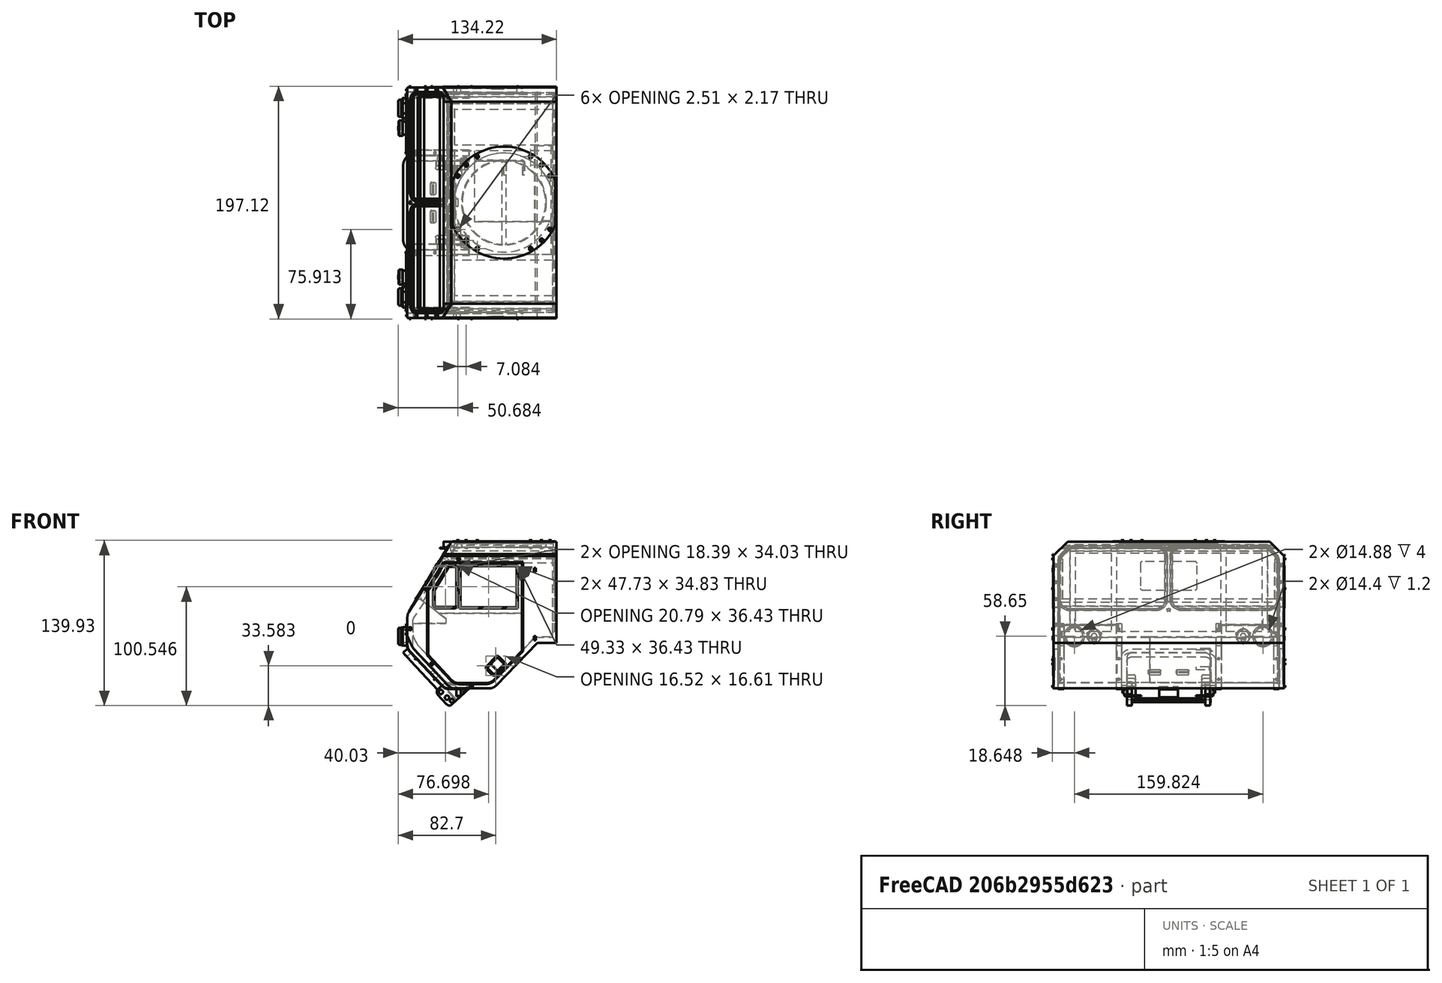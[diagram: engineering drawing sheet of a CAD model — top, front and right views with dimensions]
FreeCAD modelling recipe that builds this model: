
FCSTD DOCUMENT  (FreeCAD 0.16R6188 (Git))
Label: hemtt
License: All rights reserved
LicenseURL: http://en.wikipedia.org/wiki/All_rights_reserved
objects: Sketcher::SketchObject×10, Part::Feature×7, PartDesign::Pad×7, Part::MultiFuse×7, Part::Cut×5, Part::Box×2, Part::FeaturePython×1, Part::Mirroring×1, Part::MultiCommon×1
note: 48 computed .brp shape members not serialized (recipe doc carries the construction recipe); baked Part::Feature solids carry a one-line shape summary decoded from their .brp

FEATURE [Part::Feature] Part__Feature025  label="TELAIO HMTT025"
  shape: bbox 10530 x 1984 x 2594 mm, 1907 faces (baked)
FEATURE [Part::Feature] Part__Feature054  label="FARO CON CARTER002"
  Placement = pos=(-2615,1569,-998.9) rot=(0.707107,0,-0.707107;3.14159rad)
  shape: bbox 45 x 194.8 x 194.8 mm, 8 faces (baked)
FEATURE [Part::Feature] Part__Feature052  label="FARO CON CARTER"
  Placement = pos=(-2615,1569,998.9) rot=(-0.57735,0.57735,0.57735;4.18879rad)
  shape: bbox 45 x 194.8 x 194.8 mm, 8 faces (baked)
FEATURE [Part::Feature] Part__Feature057  label="LUCE NOTTURNA001"
  Placement = pos=(-2610,1569,-788.9) rot=(0,-1,0;1.5708rad)
  shape: bbox 99 x 164.8 x 161.2 mm, 70 faces (baked)
FEATURE [Part::Feature] Part__Feature059  label="LUCE NOTTURNA003"
  Placement = pos=(-2610,1569,788.9) rot=(0,-1,0;1.5708rad)
  shape: bbox 99 x 164.8 x 161.2 mm, 70 faces (baked)
FEATURE [Sketcher::SketchObject] Sketch
  Placement = pos=(0,-100,0) rot=(-1,0,0;4.71239rad)
  sketch-geometry (9):
    g0: LineSegment StartX=-82.586 StartY=78.6056 StartZ=0 EndX=-89.3602 EndY=104.808 EndZ=0
    g1: LineSegment StartX=-89.3602 StartY=104.808 StartZ=0 EndX=-99.131 EndY=104.808 EndZ=0
    g2: LineSegment StartX=-99.131 StartY=104.808 StartZ=0 EndX=-99.131 EndY=54.1502 EndZ=0
    g3: LineSegment StartX=-99.131 StartY=54.1502 StartZ=0 EndX=-82.0275 EndY=58.4399 EndZ=0
    g4: LineSegment StartX=-82.0275 StartY=58.4399 StartZ=0 EndX=-82.0275 EndY=60.6882 EndZ=0
    g5: LineSegment StartX=-82.0275 StartY=60.6882 StartZ=0 EndX=-90.9811 EndY=60.6882 EndZ=0
    g6: LineSegment StartX=-90.9811 StartY=60.6882 StartZ=0 EndX=-90.9811 EndY=76.174 EndZ=0
    g7: LineSegment StartX=-90.9811 StartY=76.174 StartZ=0 EndX=-82.586 EndY=76.174 EndZ=0
    g8: LineSegment StartX=-82.586 StartY=76.174 StartZ=0 EndX=-82.586 EndY=78.6056 EndZ=0
  constraints (16):
    c: Coincident(g0,g1)
    c: Horizontal(g1)
    c: Coincident(g1,g2)
    c: Vertical(g2)
    c: Coincident(g2,g3)
    c: Coincident(g3,g4)
    c: Vertical(g4)
    c: Coincident(g5,g4)
    c: Horizontal(g5)
    c: Coincident(g5,g6)
    c: Vertical(g6)
    c: Coincident(g6,g7)
    c: Horizontal(g7)
    c: Coincident(g7,g8)
    c: Coincident(g8,g0)
    c: Vertical(g8)
FEATURE [PartDesign::Pad] Pad
  Length = 210
  Length2 = 100
  Placement = pos=(0,-100,0) rot=(-1,0,0;4.71239rad)
  Reversed = true
  Sketch = -> Sketch
  Type = 0
FEATURE [Part::Feature] Part__Feature053  label="FARO CON CARTER001"
  Placement = pos=(-2615,1569,998.9) rot=(-0.57735,0.57735,0.57735;4.18879rad)
  shape: bbox 56 x 238.1 x 238.1 mm, 11 faces (baked)
FEATURE [Part::Feature] Part__Feature055  label="FARO CON CARTER003"
  Placement = pos=(-2615,1569,-998.9) rot=(0.707107,0,-0.707107;3.14159rad)
  shape: bbox 56 x 238.1 x 238.1 mm, 11 faces (baked)
FEATURE [Part::MultiFuse] Fusion
  Placement = pos=(0,0,0) rot=(1,0,0;1.5708rad)
  Shapes = -> [Part__Feature025,Part__Feature054,Part__Feature052,Part__Feature057,Part__Feature059,Part__Feature053,Part__Feature055]
FEATURE [Part::FeaturePython] Clone  label="Clone of Fusion"  # Draft clone (typed FeaturePython)
  Objects = -> [Fusion]
  Placement = pos=(120,0,-57) rot=(1,0,0;1.5708rad)
  Scale = (0.08,0.08,0.08)
FEATURE [Part::Cut] Cut
  Base = -> Clone
  Tool = -> Pad
FEATURE [Sketcher::SketchObject] Sketch001
  ExternalGeometry = -> [Cut]
  Placement = pos=(0,-97.6,0) rot=(1,0,0;1.5708rad)
  Support = -> Cut [Face30]
  sketch-geometry (11):
    g0: LineSegment StartX=-6.58206 StartY=26.7619 StartZ=0 EndX=28.4927 EndY=62.9077 EndZ=0
    g1: LineSegment StartX=28.4927 StartY=62.9077 StartZ=0 EndX=48.7262 EndY=62.9077 EndZ=0
    g2: LineSegment StartX=48.7262 StartY=62.9077 StartZ=0 EndX=48.7262 EndY=84.8524 EndZ=0
    g3: LineSegment StartX=48.7262 StartY=84.8524 StartZ=0 EndX=927.788 EndY=84.8524 EndZ=0
    g4: LineSegment StartX=927.788 StartY=84.8524 StartZ=0 EndX=927.788 EndY=-26.8754 EndZ=0
    g5: LineSegment StartX=927.788 StartY=-26.8754 StartZ=0 EndX=-68.5109 EndY=-26.8754 EndZ=0
    g6: LineSegment StartX=-68.5109 StartY=-26.8754 StartZ=0 EndX=-68.5109 EndY=-12.2515 EndZ=0
    g7: LineSegment StartX=-43.7868 StartY=10.7317 StartZ=0 EndX=-29.1551 EndY=24.3331 EndZ=0
    g8: LineSegment StartX=-29.1551 StartY=24.3331 StartZ=0 EndX=-12.3233 EndY=24.3331 EndZ=0
    g9: LineSegment StartX=-43.7868 StartY=10.7317 StartZ=0 EndX=-68.5109 EndY=-12.2515 EndZ=0
    g10: ArcOfCircle CenterX=-12.3233 CenterY=32.3331 CenterZ=0 NormalX=0 NormalY=0 NormalZ=1 Radius=8 StartAngle=4.71239 EndAngle=5.51282
  constraints (20):
    c: Coincident(g0,g1)
    c: Horizontal(g1)
    c: Coincident(g1,g2)
    c: Vertical(g2)
    c: Coincident(g2,g3)
    c: Horizontal(g3)
    c: Coincident(g3,g4)
    c: Vertical(g4)
    c: Coincident(g4,g5)
    c: Horizontal(g5)
    c: Coincident(g5,g6)
    c: Coincident(g7,g8)
    c: Horizontal(g8)
    c: Coincident(g7,g-4)
    c: Coincident(g9,g7)
    c: Coincident(g9,g6)
    c: Parallel(g9,g7)
    c: Vertical(g6)
    c: Coincident(g10,g0)
    c: Coincident(g10,g8)
FEATURE [Sketcher::SketchObject] Sketch003
  Placement = pos=(0,-101.6,0) rot=(1,0,0;1.5708rad)
  sketch-geometry (11):
    g0: LineSegment StartX=-6.58206 StartY=26.7619 StartZ=0 EndX=28.4927 EndY=62.9077 EndZ=0
    g1: LineSegment StartX=28.4927 StartY=62.9077 StartZ=0 EndX=48.7262 EndY=62.9077 EndZ=0
    g2: LineSegment StartX=48.7262 StartY=62.9077 StartZ=0 EndX=48.7262 EndY=84.8524 EndZ=0
    g3: LineSegment StartX=48.7262 StartY=84.8524 StartZ=0 EndX=927.788 EndY=84.8524 EndZ=0
    g4: LineSegment StartX=927.788 StartY=84.8524 StartZ=0 EndX=927.788 EndY=-26.8754 EndZ=0
    g5: LineSegment StartX=927.788 StartY=-26.8754 StartZ=0 EndX=-68.5109 EndY=-26.8754 EndZ=0
    g6: LineSegment StartX=-68.5109 StartY=-26.8754 StartZ=0 EndX=-68.5109 EndY=-12.2515 EndZ=0
    g7: LineSegment StartX=-43.7868 StartY=10.7317 StartZ=0 EndX=-29.1551 EndY=24.3331 EndZ=0
    g8: LineSegment StartX=-29.1551 StartY=24.3331 StartZ=0 EndX=-12.3233 EndY=24.3331 EndZ=0
    g9: LineSegment StartX=-43.7868 StartY=10.7317 StartZ=0 EndX=-68.5109 EndY=-12.2515 EndZ=0
    g10: ArcOfCircle CenterX=-12.3233 CenterY=32.3331 CenterZ=0 NormalX=0 NormalY=0 NormalZ=1 Radius=8 StartAngle=4.71239 EndAngle=5.51282
  constraints (19):
    c: Coincident(g0,g1)
    c: Horizontal(g1)
    c: Coincident(g1,g2)
    c: Vertical(g2)
    c: Coincident(g2,g3)
    c: Horizontal(g3)
    c: Coincident(g3,g4)
    c: Vertical(g4)
    c: Coincident(g4,g5)
    c: Horizontal(g5)
    c: Coincident(g5,g6)
    c: Coincident(g7,g8)
    c: Horizontal(g8)
    c: Coincident(g9,g7)
    c: Coincident(g9,g6)
    c: Parallel(g9,g7)
    c: Vertical(g6)
    c: Coincident(g10,g0)
    c: Coincident(g10,g8)
FEATURE [PartDesign::Pad] Pad001
  Length = 210
  Length2 = 100
  Placement = pos=(0,-101.6,0) rot=(1,0,0;1.5708rad)
  Reversed = true
  Sketch = -> Sketch003
  Type = 0
FEATURE [Part::Cut] Cut001
  Base = -> Cut
  Tool = -> Pad001
FEATURE [Sketcher::SketchObject] Sketch004
  ExternalGeometry = -> [Cut001]
  Placement = pos=(0,-97.6,0) rot=(1,0,0;1.5708rad)
  Support = -> Cut001 [Face749]
  sketch-geometry (24):
    g0: LineSegment StartX=11.0422 StartY=127.83 StartZ=0 EndX=-36.6868 EndY=127.83 EndZ=0
    g1: LineSegment StartX=-36.6868 StartY=127.83 StartZ=0 EndX=-36.6868 EndY=93.0022 EndZ=0
    g2: LineSegment StartX=-36.6868 StartY=93.0022 StartZ=0 EndX=11.0422 EndY=93.0022 EndZ=0
    g3: LineSegment StartX=11.0422 StartY=93.0022 StartZ=0 EndX=11.0422 EndY=127.83 EndZ=0
    g4: LineSegment StartX=-45.8126 StartY=127.43 StartZ=0 EndX=-41.4972 EndY=127.43 EndZ=0
    g5: ArcOfCircle CenterX=-45.8126 CenterY=126.23 CenterZ=0 NormalX=0 NormalY=0 NormalZ=1 Radius=1.2 StartAngle=1.5708 EndAngle=2.59824
    g6: ArcOfCircle CenterX=-41.4972 CenterY=126.23 CenterZ=0 NormalX=0 NormalY=0 NormalZ=1 Radius=1.2 StartAngle=0 EndAngle=1.5708
    g7: LineSegment StartX=-46.8398 StartY=126.851 StartZ=0 EndX=-58.5097 EndY=107.529 EndZ=0
    g8: LineSegment StartX=-40.2972 StartY=126.23 StartZ=0 EndX=-40.2972 EndY=94.6022 EndZ=0
    g9: LineSegment StartX=-58.6825 StartY=106.909 StartZ=0 EndX=-58.6825 EndY=94.6022 EndZ=0
    g10: LineSegment StartX=-57.4825 StartY=93.4022 StartZ=0 EndX=-41.4972 EndY=93.4022 EndZ=0
    g11: ArcOfCircle CenterX=-57.4825 CenterY=106.909 CenterZ=0 NormalX=0 NormalY=0 NormalZ=1 Radius=1.2 StartAngle=2.59824 EndAngle=3.14159
    g12: ArcOfCircle CenterX=-41.4972 CenterY=94.6022 CenterZ=0 NormalX=0 NormalY=0 NormalZ=1 Radius=1.2 StartAngle=4.71239 EndAngle=6.28319
    g13: ArcOfCircle CenterX=-57.4825 CenterY=94.6022 CenterZ=0 NormalX=0 NormalY=0 NormalZ=1 Radius=1.2 StartAngle=3.14159 EndAngle=4.71239
    g14: LineSegment StartX=-63.6825 StartY=88.0022 StartZ=0 EndX=-63.6825 EndY=108.636 EndZ=0
    g15: LineSegment StartX=-63.6825 StartY=108.636 StartZ=0 EndX=-49.0694 EndY=132.83 EndZ=0
    g16: LineSegment StartX=-49.0694 StartY=132.83 StartZ=0 EndX=16.0422 EndY=132.83 EndZ=0
    g17: LineSegment StartX=16.0422 StartY=132.83 StartZ=0 EndX=16.0422 EndY=88.0022 EndZ=0
    g18: LineSegment StartX=16.0422 StartY=88.0022 StartZ=0 EndX=-63.6825 EndY=88.0022 EndZ=0
    g19: LineSegment [constr] StartX=-36.6868 StartY=93.0022 StartZ=0 EndX=-36.6868 EndY=88.0022 EndZ=0
    g20: LineSegment [constr] StartX=-36.6868 StartY=127.83 StartZ=0 EndX=-36.6868 EndY=132.83 EndZ=0
    g21: LineSegment [constr] StartX=-46.8398 StartY=126.851 StartZ=0 EndX=-51.1197 EndY=129.436 EndZ=0
    g22: LineSegment [constr] StartX=11.0422 StartY=127.83 StartZ=0 EndX=16.0422 EndY=127.83 EndZ=0
    g23: LineSegment [constr] StartX=-58.6825 StartY=106.909 StartZ=0 EndX=-63.6825 EndY=106.909 EndZ=0
  constraints (65):
    c: Coincident(g0,g1)
    c: Coincident(g1,g2)
    c: Coincident(g2,g3)
    c: Coincident(g3,g0)
    c: Horizontal(g0)
    c: Horizontal(g2)
    c: Vertical(g1)
    c: Vertical(g3)
    c: Coincident(g0,g-9)
    c: Coincident(g1,g-8)
    c: Coincident(g-4,g4)
    c: Coincident(g-3,g4)
    c: Coincident(g5,g-3)
    c: Coincident(g5,g4)
    c: Coincident(g5,g-3)
    c: Coincident(g6,g-4)
    c: Coincident(g6,g4)
    c: Coincident(g6,g-4)
    c: Coincident(g7,g-6)
    c: Coincident(g5,g7)
    c: Coincident(g8,g6)
    c: Coincident(g8,g-7)
    c: Coincident(g9,g-6)
    c: Coincident(g9,g-5)
    c: Coincident(g10,g-5)
    c: Coincident(g10,g-7)
    c: Coincident(g11,g-6)
    c: Coincident(g11,g7)
    c: Coincident(g11,g9)
    c: Coincident(g12,g-7)
    c: Coincident(g12,g8)
    c: Coincident(g12,g10)
    c: Coincident(g13,g-5)
    c: Coincident(g13,g9)
    c: Coincident(g13,g10)
    c: Vertical(g14)
    c: Coincident(g14,g15)
    c: Coincident(g15,g16)
    c: Horizontal(g16)
    c: Coincident(g16,g17)
    c: Vertical(g17)
    c: Coincident(g17,g18)
    c: Coincident(g18,g14)
    c: Horizontal(g18)
    c: Coincident(g19,g1)
    c: PointOnObject(g19,g18)
    c: Vertical(g19)
    c: Coincident(g20,g0)
    c: PointOnObject(g20,g16)
    c: Vertical(g20)
    c: Coincident(g21,g5)
    c: PointOnObject(g21,g15)
    c: Coincident(g22,g0)
    c: PointOnObject(g22,g17)
    c: Horizontal(g22)
    c: Coincident(g23,g9)
    c: PointOnObject(g23,g14)
    c: Horizontal(g23)
    c: Perpendicular(g21,g15)
    c: Equal(g23,g21)
    c: Equal(g21,g20)
    c: Equal(g20,g22)
    c: Equal(g22,g19)
    c: Parallel(g15,g7)
    c: Distance(g20) = 5
FEATURE [Sketcher::SketchObject] Sketch007
  Placement = pos=(0,-97.5,0) rot=(1,0,0;1.5708rad)
  sketch-geometry (24):
    g0: LineSegment StartX=11.0422 StartY=127.83 StartZ=0 EndX=-36.6868 EndY=127.83 EndZ=0
    g1: LineSegment StartX=-36.6868 StartY=127.83 StartZ=0 EndX=-36.6868 EndY=93.0022 EndZ=0
    g2: LineSegment StartX=-36.6868 StartY=93.0022 StartZ=0 EndX=11.0422 EndY=93.0022 EndZ=0
    g3: LineSegment StartX=11.0422 StartY=93.0022 StartZ=0 EndX=11.0422 EndY=127.83 EndZ=0
    g4: LineSegment StartX=-45.8126 StartY=127.43 StartZ=0 EndX=-41.4972 EndY=127.43 EndZ=0
    g5: ArcOfCircle CenterX=-45.8126 CenterY=126.23 CenterZ=0 NormalX=0 NormalY=0 NormalZ=1 Radius=1.2 StartAngle=1.5708 EndAngle=2.59824
    g6: ArcOfCircle CenterX=-41.4972 CenterY=126.23 CenterZ=0 NormalX=0 NormalY=0 NormalZ=1 Radius=1.2 StartAngle=0 EndAngle=1.5708
    g7: LineSegment StartX=-46.8398 StartY=126.851 StartZ=0 EndX=-58.5097 EndY=107.529 EndZ=0
    g8: LineSegment StartX=-40.2972 StartY=126.23 StartZ=0 EndX=-40.2972 EndY=94.6022 EndZ=0
    g9: LineSegment StartX=-58.6825 StartY=106.909 StartZ=0 EndX=-58.6825 EndY=94.6022 EndZ=0
    g10: LineSegment StartX=-57.4825 StartY=93.4022 StartZ=0 EndX=-41.4972 EndY=93.4022 EndZ=0
    g11: ArcOfCircle CenterX=-57.4825 CenterY=106.909 CenterZ=0 NormalX=0 NormalY=0 NormalZ=1 Radius=1.2 StartAngle=2.59824 EndAngle=3.14159
    g12: ArcOfCircle CenterX=-41.4972 CenterY=94.6022 CenterZ=0 NormalX=0 NormalY=0 NormalZ=1 Radius=1.2 StartAngle=4.71239 EndAngle=6.28319
    g13: ArcOfCircle CenterX=-57.4825 CenterY=94.6022 CenterZ=0 NormalX=0 NormalY=0 NormalZ=1 Radius=1.2 StartAngle=3.14159 EndAngle=4.71239
    g14: LineSegment StartX=-63.6825 StartY=88.0022 StartZ=0 EndX=-63.6825 EndY=108.636 EndZ=0
    g15: LineSegment StartX=-63.6825 StartY=108.636 StartZ=0 EndX=-49.0694 EndY=132.83 EndZ=0
    g16: LineSegment StartX=-49.0694 StartY=132.83 StartZ=0 EndX=16.0422 EndY=132.83 EndZ=0
    g17: LineSegment StartX=16.0422 StartY=132.83 StartZ=0 EndX=16.0422 EndY=88.0022 EndZ=0
    g18: LineSegment StartX=16.0422 StartY=88.0022 StartZ=0 EndX=-63.6825 EndY=88.0022 EndZ=0
    g19: LineSegment [constr] StartX=-36.6868 StartY=93.0022 StartZ=0 EndX=-36.6868 EndY=88.0022 EndZ=0
    g20: LineSegment [constr] StartX=-36.6868 StartY=127.83 StartZ=0 EndX=-36.6868 EndY=132.83 EndZ=0
    g21: LineSegment [constr] StartX=-46.8398 StartY=126.851 StartZ=0 EndX=-51.1197 EndY=129.436 EndZ=0
    g22: LineSegment [constr] StartX=11.0422 StartY=127.83 StartZ=0 EndX=16.0422 EndY=127.83 EndZ=0
    g23: LineSegment [constr] StartX=-58.6825 StartY=106.909 StartZ=0 EndX=-63.6825 EndY=106.909 EndZ=0
  constraints (48):
    c: Coincident(g0,g1)
    c: Coincident(g1,g2)
    c: Coincident(g2,g3)
    c: Coincident(g3,g0)
    c: Horizontal(g0)
    c: Horizontal(g2)
    c: Vertical(g1)
    c: Vertical(g3)
    c: Coincident(g5,g4)
    c: Coincident(g6,g4)
    c: Coincident(g5,g7)
    c: Coincident(g8,g6)
    c: Coincident(g11,g7)
    c: Coincident(g11,g9)
    c: Coincident(g12,g8)
    c: Coincident(g12,g10)
    c: Coincident(g13,g9)
    c: Coincident(g13,g10)
    c: Vertical(g14)
    c: Coincident(g14,g15)
    c: Coincident(g15,g16)
    c: Horizontal(g16)
    c: Coincident(g16,g17)
    c: Vertical(g17)
    c: Coincident(g17,g18)
    c: Coincident(g18,g14)
    c: Horizontal(g18)
    c: Coincident(g19,g1)
    c: PointOnObject(g19,g18)
    c: Vertical(g19)
    c: Coincident(g20,g0)
    c: PointOnObject(g20,g16)
    c: Vertical(g20)
    c: Coincident(g21,g5)
    c: PointOnObject(g21,g15)
    c: Coincident(g22,g0)
    c: PointOnObject(g22,g17)
    c: Horizontal(g22)
    c: Coincident(g23,g9)
    c: PointOnObject(g23,g14)
    c: Horizontal(g23)
    c: Perpendicular(g21,g15)
    c: Equal(g23,g21)
    c: Equal(g21,g20)
    c: Equal(g20,g22)
    c: Equal(g22,g19)
    c: Parallel(g15,g7)
    c: Distance(g20) = 5
FEATURE [PartDesign::Pad] Pad002
  Length = 5
  Length2 = 100
  Placement = pos=(0,-97.5,0) rot=(1,0,0;1.5708rad)
  Reversed = true
  Sketch = -> Sketch007
  Type = 0
FEATURE [Part::Mirroring] Part__Mirroring  label="Pad002 (Mirror #1)"
  Base = (-23.8002,0,110.436)
  Normal = (0,1,-1.19209e-07)
  Source = -> Pad002
FEATURE [Sketcher::SketchObject] Sketch008
  Placement = pos=(0,97,0) rot=(-1,0,0;4.71239rad)
  sketch-geometry (4):
    g0: LineSegment StartX=-80.0736 StartY=88.4835 StartZ=0 EndX=-76.6552 EndY=94.075 EndZ=0
    g1: LineSegment StartX=-76.6552 StartY=94.075 StartZ=0 EndX=-76.2478 EndY=94.075 EndZ=0
    g2: LineSegment StartX=-76.2478 StartY=94.075 StartZ=0 EndX=-76.2478 EndY=86.197 EndZ=0
    g3: LineSegment StartX=-76.2478 StartY=86.197 StartZ=0 EndX=-80.0736 EndY=88.4835 EndZ=0
  constraints (6):
    c: Coincident(g0,g1)
    c: Horizontal(g1)
    c: Coincident(g1,g2)
    c: Vertical(g2)
    c: Coincident(g2,g3)
    c: Coincident(g3,g0)
FEATURE [PartDesign::Pad] Pad003
  Length = 194
  Length2 = 100
  Placement = pos=(0,97,0) rot=(-1,0,0;4.71239rad)
  Sketch = -> Sketch008
  Type = 0
FEATURE [Sketcher::SketchObject] Sketch009
  Placement = pos=(0,-3.12,0) rot=(1,0,0;1.5708rad)
  sketch-geometry (7):
    g0: LineSegment StartX=-71.1705 StartY=93.0565 StartZ=0 EndX=-38.082 EndY=147.839 EndZ=0
    g1: LineSegment StartX=-38.082 StartY=147.839 StartZ=0 EndX=-43.9233 EndY=147.839 EndZ=0
    g2: LineSegment StartX=-43.9233 StartY=147.839 StartZ=0 EndX=-50.9103 EndY=136.271 EndZ=0
    g3: LineSegment [constr] StartX=-43.9233 StartY=147.839 StartZ=0 EndX=-39.6433 EndY=145.254 EndZ=0
    g4: LineSegment StartX=-72.8757 StartY=99.9043 StartZ=0 EndX=-77.0118 EndY=93.0565 EndZ=0
    g5: LineSegment StartX=-77.0118 StartY=93.0565 StartZ=0 EndX=-71.1705 EndY=93.0565 EndZ=0
    g6: LineSegment StartX=-50.9103 StartY=136.271 StartZ=0 EndX=-72.8757 EndY=99.9043 EndZ=0
  constraints (15):
    c: Coincident(g0,g1)
    c: Horizontal(g1)
    c: Coincident(g1,g2)
    c: Coincident(g3,g1)
    c: PointOnObject(g3,g0)
    c: Perpendicular(g0,g3)
    c: Distance(g3) = 5
    c: Coincident(g4,g5)
    c: Coincident(g5,g0)
    c: Horizontal(g5)
    c: Parallel(g4,g0)
    c: Distance(g0) = 64
    c: Distance(g4) = 8
    c: Coincident(g6,g2)
    c: Coincident(g6,g4)
FEATURE [Sketcher::SketchObject] Sketch013
  Placement = pos=(0,-3.12,0) rot=(1,0,0;1.5708rad)
  sketch-geometry (7):
    g0: LineSegment StartX=-71.1705 StartY=93.0565 StartZ=0 EndX=-38.082 EndY=147.839 EndZ=0
    g1: LineSegment StartX=-38.082 StartY=147.839 StartZ=0 EndX=-43.9233 EndY=147.839 EndZ=0
    g2: LineSegment StartX=-43.9233 StartY=147.839 StartZ=0 EndX=-50.9103 EndY=136.271 EndZ=0
    g3: LineSegment [constr] StartX=-43.9233 StartY=147.839 StartZ=0 EndX=-39.6433 EndY=145.254 EndZ=0
    g4: LineSegment StartX=-72.8757 StartY=99.9043 StartZ=0 EndX=-77.0118 EndY=93.0565 EndZ=0
    g5: LineSegment StartX=-77.0118 StartY=93.0565 StartZ=0 EndX=-71.1705 EndY=93.0565 EndZ=0
    g6: LineSegment StartX=-50.9103 StartY=136.271 StartZ=0 EndX=-72.8757 EndY=99.9043 EndZ=0
  constraints (15):
    c: Coincident(g0,g1)
    c: Horizontal(g1)
    c: Coincident(g1,g2)
    c: Coincident(g3,g1)
    c: PointOnObject(g3,g0)
    c: Perpendicular(g0,g3)
    c: Distance(g3) = 5
    c: Coincident(g4,g5)
    c: Coincident(g5,g0)
    c: Horizontal(g5)
    c: Parallel(g4,g0)
    c: Distance(g0) = 64
    c: Distance(g4) = 8
    c: Coincident(g6,g2)
    c: Coincident(g6,g4)
FEATURE [PartDesign::Pad] Pad004
  Length = 6.25
  Length2 = 100
  Placement = pos=(0,-3.12,0) rot=(1,0,0;1.5708rad)
  Reversed = true
  Sketch = -> Sketch013
  Type = 0
FEATURE [Sketcher::SketchObject] Sketch014
  Placement = pos=(0,92,0) rot=(-1,0,0;4.71239rad)
  sketch-geometry (12):
    g0: LineSegment StartX=-77.405 StartY=80.1635 StartZ=0 EndX=-77.405 EndY=61.0528 EndZ=0
    g1: LineSegment StartX=-76.642 StartY=59.1374 StartZ=0 EndX=-49.246 EndY=30.2051 EndZ=0
    g2: LineSegment StartX=-46.63 StartY=29.0795 StartZ=0 EndX=-14.2284 EndY=29.0795 EndZ=0
    g3: LineSegment StartX=-8.95205 StartY=31.3185 StartZ=0 EndX=26.2884 EndY=67.7935 EndZ=0
    g4: LineSegment StartX=26.2884 StartY=67.7935 StartZ=0 EndX=40.2605 EndY=67.7935 EndZ=0
    g5: LineSegment StartX=40.2605 StartY=67.7935 StartZ=0 EndX=40.2605 EndY=81.3532 EndZ=0
    g6: LineSegment StartX=40.2605 StartY=81.3532 StartZ=0 EndX=-62.0229 EndY=105.665 EndZ=0
    g7: LineSegment StartX=-62.0229 StartY=105.665 StartZ=0 EndX=-76.0046 EndY=84.7738 EndZ=0
    g8: ArcOfCircle CenterX=-74.6192 CenterY=61.0528 CenterZ=0 NormalX=0 NormalY=0 NormalZ=1 Radius=2.78585 StartAngle=3.14159 EndAngle=3.89973
    g9: ArcOfCircle CenterX=-46.63 CenterY=32.6822 CenterZ=0 NormalX=0 NormalY=0 NormalZ=1 Radius=3.60261 StartAngle=3.89973 EndAngle=4.71239
    g10: ArcOfCircle CenterX=-14.2284 CenterY=36.4162 CenterZ=0 NormalX=0 NormalY=0 NormalZ=1 Radius=7.33669 StartAngle=4.71239 EndAngle=5.515
    g11: ArcOfCircle CenterX=-69.1161 CenterY=80.1635 CenterZ=0 NormalX=0 NormalY=0 NormalZ=1 Radius=8.28891 StartAngle=2.55179 EndAngle=3.14159
  constraints (16):
    c: Vertical(g0)
    c: Horizontal(g2)
    c: Coincident(g3,g4)
    c: Horizontal(g4)
    c: Coincident(g4,g5)
    c: Vertical(g5)
    c: Coincident(g5,g6)
    c: Coincident(g6,g7)
    c: Tangent(g0,g8) = -1.5708
    c: Tangent(g1,g8) = -1.5708
    c: Tangent(g1,g9) = -1.5708
    c: Tangent(g2,g9) = -1.5708
    c: Tangent(g2,g10) = -1.5708
    c: Tangent(g3,g10) = -1.5708
    c: Tangent(g0,g11) = -1.5708
    c: Tangent(g7,g11) = -1.5708
FEATURE [PartDesign::Pad] Pad005
  Length = 184
  Length2 = 100
  Placement = pos=(0,92,0) rot=(-1,0,0;4.71239rad)
  Sketch = -> Sketch014
  Type = 0
FEATURE [Part::MultiFuse] Fusion002
  Shapes = -> [Part__Mirroring,Pad002]
FEATURE [Sketcher::SketchObject] Sketch015
  sketch-geometry (8):
    g0: LineSegment StartX=14.281 StartY=-98.1827 StartZ=0 EndX=28.4886 EndY=-98.1827 EndZ=0
    g1: LineSegment StartX=28.4886 StartY=-98.1827 StartZ=0 EndX=28.4886 EndY=-104.667 EndZ=0
    g2: LineSegment StartX=28.4886 StartY=-104.667 StartZ=0 EndX=14.281 EndY=-104.667 EndZ=0
    g3: LineSegment StartX=14.281 StartY=-104.667 StartZ=0 EndX=14.281 EndY=-98.1827 EndZ=0
    g4: LineSegment StartX=14.4041 StartY=104.392 StartZ=0 EndX=27.8033 EndY=104.392 EndZ=0
    g5: LineSegment StartX=27.8033 StartY=104.392 StartZ=0 EndX=27.8033 EndY=98.1857 EndZ=0
    g6: LineSegment StartX=27.8033 StartY=98.1857 StartZ=0 EndX=14.4041 EndY=98.1857 EndZ=0
    g7: LineSegment StartX=14.4041 StartY=98.1857 StartZ=0 EndX=14.4041 EndY=104.392 EndZ=0
  constraints (16):
    c: Coincident(g0,g1)
    c: Coincident(g1,g2)
    c: Coincident(g2,g3)
    c: Coincident(g3,g0)
    c: Horizontal(g0)
    c: Horizontal(g2)
    c: Vertical(g1)
    c: Vertical(g3)
    c: Coincident(g4,g5)
    c: Coincident(g5,g6)
    c: Coincident(g6,g7)
    c: Coincident(g7,g4)
    c: Horizontal(g4)
    c: Horizontal(g6)
    c: Vertical(g5)
    c: Vertical(g7)
FEATURE [PartDesign::Pad] Pad006
  Length = 185
  Length2 = 100
  Sketch = -> Sketch015
  Type = 0
FEATURE [Part::Cut] Cut002
  Base = -> Cut001
  Tool = -> Pad006
FEATURE [Part::Cut] Cut003
  Base = -> Cut002
  Tool = -> Pad005
FEATURE [Part::MultiFuse] Fusion003
  Shapes = -> [Fusion002,Cut003]
FEATURE [Part::Box] Box  label="Cube"
  Height = 90
  Length = 300
  Placement = pos=(-150,-150,82) rot=(0,0,1;0rad)
  Width = 300
FEATURE [Part::MultiFuse] Fusion004
  Shapes = -> [Fusion002,Cut003]
FEATURE [Part::Box] Box001  label="Cube001"
  Height = 90
  Length = 300
  Placement = pos=(-150,-150,81) rot=(0,0,1;0rad)
  Width = 300
FEATURE [Part::Cut] Cut004
  Base = -> Fusion003
  Tool = -> Box
FEATURE [Part::MultiCommon] Common
  Shapes = -> [Fusion004,Box001]
FEATURE [Part::MultiFuse] Fusion005
  Shapes = -> [Cut004,Common]
FEATURE [Part::MultiFuse] Fusion006
  Shapes = -> [Pad003,Pad004]
FEATURE [Part::MultiFuse] Fusion007
  Shapes = -> [Fusion005,Fusion006]
